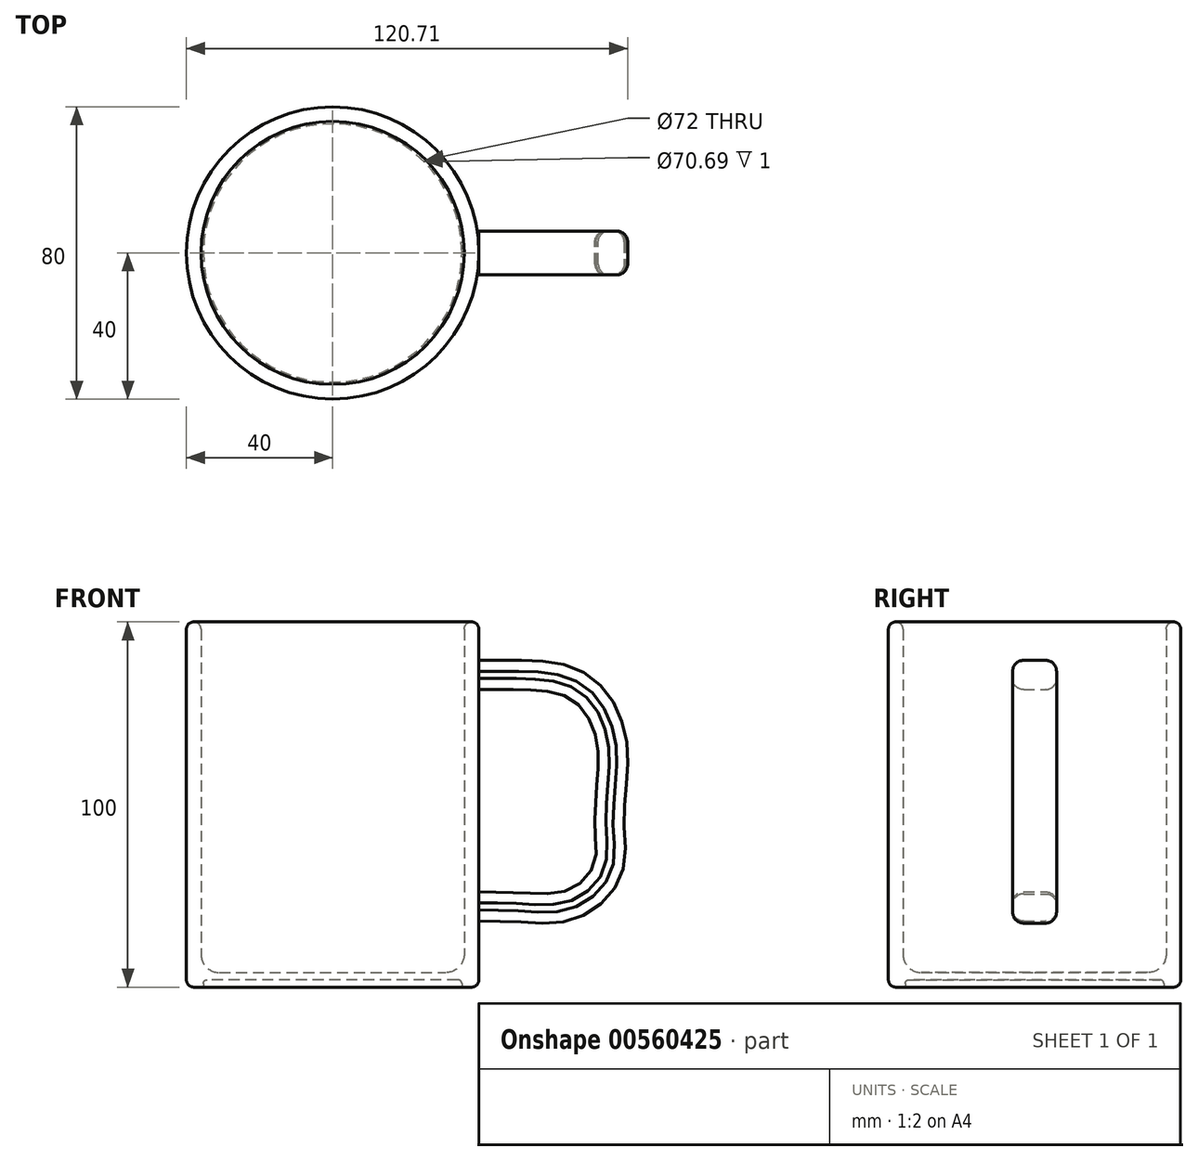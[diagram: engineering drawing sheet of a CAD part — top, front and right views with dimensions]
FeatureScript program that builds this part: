
annotation { "Feature Type Name" : "Feature", "Feature Type Description" : "" }
export const myFeature = defineFeature(function(context is Context, id is Id, definition is map)
    precondition{}
    {
        {
            var Q0;
            Q0=qCreatedBy(makeId("Front.planeOp"),FACE);
            var sketch = newSketch(context, id + "F0", { "sketchPlane" : qUnion([Q0])});
            skLineSegment(sketch, "E0.bottom", {"start": v(0, 0) * mm, "end": v(40, 0) * mm});
            skLineSegment(sketch, "E0.top", {"start": v(0, 100) * mm, "end": v(40, 100) * mm});
            skLineSegment(sketch, "E0.left", {"start": v(0, 0) * mm, "end": v(0, 100) * mm});
            skLineSegment(sketch, "E0.right", {"start": v(40, 0) * mm, "end": v(40, 100) * mm});
            skFitSpline(sketch, "E1", {"points": [v(31.21, 81.47) * mm, v(49.43, 81.47) * mm, v(64.9, 79.06) * mm, v(71.77, 69.44) * mm, v(72.45, 57.4) * mm, v(71.77, 43.32) * mm, v(71.42, 33.35) * mm, v(64.2, 26.48) * mm, v(52.18, 25.8) * mm, v(32.59, 26.13) * mm], "startDerivative": vector(140.72, 0.24) * mm, "endDerivative": vector(-154.35, 0.43) * mm});
            skFitSpline(sketch, "E2.0", {"points": [v(31.2, 89.47) * mm, v(32.66, 89.47) * mm, v(35.6, 89.47) * mm, v(39.27, 89.48) * mm, v(42.22, 89.48) * mm, v(44.44, 89.48) * mm, v(46.66, 89.47) * mm, v(48.52, 89.47) * mm, v(50, 89.46) * mm, v(51.15, 89.46) * mm, v(52.32, 89.45) * mm, v(53.91, 89.41) * mm, v(55.95, 89.33) * mm, v(58.48, 89.13) * mm, v(61.07, 88.77) * mm, v(63.29, 88.27) * mm, v(65.09, 87.71) * mm, v(66.45, 87.2) * mm, v(67.58, 86.7) * mm, v(68.48, 86.22) * mm, v(69.38, 85.7) * mm, v(70.45, 85.01) * mm, v(71.64, 84.1) * mm, v(72.74, 83.13) * mm, v(74.08, 81.76) * mm, v(75.55, 79.95) * mm, v(77, 77.66) * mm, v(78.17, 75.32) * mm, v(79.1, 72.93) * mm, v(79.78, 70.54) * mm, v(80.4, 67.39) * mm, v(80.7, 63.6) * mm, v(80.63, 60.08) * mm, v(80.5, 57.7) * mm, v(80.4, 56.38) * mm, v(80.25, 54.39) * mm, v(80.07, 52.1) * mm, v(79.9, 49.56) * mm, v(79.8, 47.74) * mm, v(79.74, 46.3) * mm, v(79.73, 45.2) * mm, v(79.74, 44.53) * mm, v(79.75, 44.02) * mm, v(79.76, 43.65) * mm, v(79.77, 43.29) * mm, v(79.8, 42.78) * mm, v(79.84, 42.11) * mm, v(79.92, 40.99) * mm, v(80.03, 39.45) * mm, v(80.1, 37.36) * mm, v(80.01, 35.37) * mm, v(79.77, 33.64) * mm, v(79.48, 32.28) * mm, v(79.13, 31.12) * mm, v(78.78, 30.18) * mm, v(78.39, 29.27) * mm, v(77.84, 28.19) * mm, v(76.85, 26.57) * mm, v(75.43, 24.73) * mm, v(73.48, 22.81) * mm, v(71.68, 21.43) * mm, v(70.13, 20.46) * mm, v(68.92, 19.8) * mm, v(67.66, 19.23) * mm, v(66.34, 18.73) * mm, v(65.03, 18.34) * mm, v(63.31, 17.94) * mm, v(61.23, 17.64) * mm, v(58.89, 17.52) * mm, v(56.69, 17.54) * mm, v(54.6, 17.64) * mm, v(53.1, 17.73) * mm, v(52.13, 17.78) * mm, v(51.48, 17.82) * mm, v(50.67, 17.86) * mm, v(49.66, 17.9) * mm, v(48.28, 17.95) * mm, v(45.8, 18.02) * mm, v(42.06, 18.09) * mm, v(37.38, 18.12) * mm, v(34.17, 18.13) * mm, v(32.56, 18.13) * mm]});
            skLineSegment(sketch, "E3", {"start": v(31.2, 89.47) * mm, "end": v(31.21, 81.47) * mm});
            skLineSegment(sketch, "E4", {"start": v(32.59, 26.13) * mm, "end": v(32.56, 18.13) * mm});
            skSolve(sketch);
        }
        {
            var Q0;
            {var subQ9=sQuery(id+"F0.wireOp",EDGE,"E0.bottom");Q0=makeQuery(id+"F0.imprint","IMPRINT",FACE,{"disambiguationData":[TD([[makeQuery(id+"F0.imprint","IMPRINT",EDGE,{"derivedFrom":subQ9}),1.0]])]});}
            var Q1;
            {var subQ5=sQuery(id+"F0.wireOp",EDGE,"E3");Q1=makeQuery(id+"F0.imprint","IMPRINT",FACE,{"disambiguationData":[TD([[makeQuery(id+"F0.imprint","IMPRINT",EDGE,{"derivedFrom":subQ5}),1.0]])]});}
            var Q2;
            {var subQ5=sQuery(id+"F0.wireOp",EDGE,"E4");Q2=makeQuery(id+"F0.imprint","IMPRINT",FACE,{"disambiguationData":[TD([[makeQuery(id+"F0.imprint","IMPRINT",EDGE,{"derivedFrom":subQ5}),1.0]])]});}
            var Q3;
            Q3=sQuery(id+"F0.wireOp",EDGE,"E0.left");
            revolve(context, id + "F1", {"entities" : qUnion([Q0, Q1, Q2]), "axis" : qUnion([Q3]), "revolveType" : RevolveType.FULL});
        }
        {
            var Q0;
            {var subQ0=sQuery(id+"F0.wireOp",EDGE,"E2.0");var subQ1=sQuery(id+"F0.wireOp",EDGE,"E0.right");var subQ2=makeQuery(id+"F0.imprint","INTERSECT",VERTEX,{"disambiguationData":[OD(0.0)],"derivedFrom":[subQ1,subQ0]});Q0=makeQuery(id+"F0.imprint","IMPRINT",FACE,{"disambiguationData":[TD([[makeQuery(id+"F0.imprint","IMPRINT",EDGE,{"disambiguationData":[TD([[subQ2,-1.0]])],"derivedFrom":subQ1}),-1.0]])]});}
            extrude(context, id + "F2", {"entities" : qUnion([Q0]), "operationType" : NewBodyOperationType.ADD, "endBound" : BoundingType.SYMMETRIC, "depth" : 12 * mm, "offsetDistance" : 25 * mm});
        }
        {
            var Q0;
            Q0=makeQuery(id+"F2.opExtrude","CAP_EDGE",EDGE,{"disambiguationData":[OSD([sQuery(id+"F0.wireOp",EDGE,"E2.0")])],"isStart":false});
            var Q1;
            Q1=makeQuery(id+"F2.opExtrude","CAP_EDGE",EDGE,{"disambiguationData":[OSD([sQuery(id+"F0.wireOp",EDGE,"E1")])],"isStart":false});
            var Q2;
            Q2=makeQuery(id+"F2.opExtrude","CAP_EDGE",EDGE,{"disambiguationData":[OSD([sQuery(id+"F0.wireOp",EDGE,"E2.0")])],"isStart":true});
            var Q3;
            Q3=makeQuery(id+"F2.opExtrude","CAP_EDGE",EDGE,{"disambiguationData":[OSD([sQuery(id+"F0.wireOp",EDGE,"E1")])],"isStart":true});
            fillet(context, id + "F3", {"entities" : qUnion([Q0, Q1, Q2, Q3]), "radius" : 3 * mm, "tangentPropagation" : true, "allowEdgeOverflow" : false});
        }
        {
            var Q0;
            Q0=makeQuery(id+"F1.opRevolve","SWEPT_FACE",FACE,{"disambiguationData":[OSD([sQuery(id+"F0.wireOp",EDGE,"E0.top")])]});
            shell(context, id + "F4", {"entities" : qUnion([Q0]), "thickness" : 4 * mm});
        }
        {
            var Q0;
            Q0=makeQuery(id+"F4.opShell","OFFSET_EDGE",EDGE,{"disambiguationData":[OSD([sQuery(id+"F0.wireOp",EDGE,"E0.top"),sQuery(id+"F0.wireOp",EDGE,"E0.right")])]});
            var Q1;
            Q1=makeQuery(id+"F1.opRevolve","SWEPT_EDGE",EDGE,{"disambiguationData":[OSD([sQuery(id+"F0.wireOp",EDGE,"E0.top"),sQuery(id+"F0.wireOp",EDGE,"E0.right")])]});
            fillet(context, id + "F5", {"entities" : qUnion([Q0, Q1]), "radius" : 2 * mm, "tangentPropagation" : true, "allowEdgeOverflow" : false});
        }
        {
            var Q0;
            Q0=makeQuery(id+"F4.opShell","OFFSET_EDGE",EDGE,{"disambiguationData":[OSD([sQuery(id+"F0.wireOp",EDGE,"E0.bottom"),sQuery(id+"F0.wireOp",EDGE,"E0.right")])]});
            fillet(context, id + "F6", {"entities" : qUnion([Q0]), "radius" : 5 * mm, "tangentPropagation" : true, "allowEdgeOverflow" : false});
        }
        {
            var Q0;
            Q0=qCreatedBy(makeId("Top.planeOp"),FACE);
            var sketch = newSketch(context, id + "F7", { "sketchPlane" : qUnion([Q0])});
            skCircle(sketch, "E5", {"center": v(0, 0) * mm, "radius": 35.35 * mm});
            skSolve(sketch);
        }
        {
            var Q0;
            Q0=makeQuery(id+"F7.imprint","IMPRINT",FACE,{"disambiguationData":[TD([[makeQuery(id+"F7.imprint","IMPRINT",EDGE,{"derivedFrom":sQuery(id+"F7.wireOp",EDGE,"E5")}),1.0]])]});
            var Q1;
            Q1=sQuery(id+"F7.wireOp",EDGE,"E5");
            extrude(context, id + "F8", {"entities" : qUnion([Q0]), "operationType" : NewBodyOperationType.REMOVE, "surfaceEntities" : qUnion([Q1]), "depth" : 2 * mm, "offsetDistance" : 25 * mm});
        }
        {
            var Q0;
            Q0=makeQuery(id+"F8.boolean.opBoolean","COPY",EDGE,{"derivedFrom":makeQuery(id+"F8.opExtrude","CAP_EDGE",EDGE,{"disambiguationData":[OSD([sQuery(id+"F7.wireOp",EDGE,"E5")])],"isStart":false})});
            var Q1;
            Q1=makeQuery(id+"F8.boolean.opBoolean","COPY",EDGE,{"derivedFrom":makeQuery(id+"F8.opExtrude","CAP_EDGE",EDGE,{"disambiguationData":[OSD([sQuery(id+"F7.wireOp",EDGE,"E5")])],"isStart":true})});
            fillet(context, id + "F9", {"entities" : qUnion([Q0, Q1]), "radius" : 1 * mm, "tangentPropagation" : true, "allowEdgeOverflow" : false});
        }
        {
            var Q0;
            Q0=makeQuery(id+"F9.opFillet","BLEND_EDGE",EDGE,{"blendedFrom":[makeQuery(id+"F8.boolean.opBoolean","COPY",EDGE,{"derivedFrom":makeQuery(id+"F8.opExtrude","CAP_EDGE",EDGE,{"disambiguationData":[OSD([sQuery(id+"F7.wireOp",EDGE,"E5")])],"isStart":true})}),makeQuery(id+"F1.opRevolve","SWEPT_FACE",FACE,{"disambiguationData":[OSD([sQuery(id+"F0.wireOp",EDGE,"E0.bottom")])]})],"blendedInto":[makeQuery(id+"F1.opRevolve","SWEPT_FACE",FACE,{"disambiguationData":[OSD([sQuery(id+"F0.wireOp",EDGE,"E0.bottom")])]})]});
            var Q1;
            Q1=makeQuery(id+"F1.opRevolve","SWEPT_EDGE",EDGE,{"disambiguationData":[OSD([sQuery(id+"F0.wireOp",EDGE,"E0.bottom"),sQuery(id+"F0.wireOp",EDGE,"E0.right")])]});
            fillet(context, id + "F10", {"entities" : qUnion([Q0, Q1]), "radius" : 2 * mm, "tangentPropagation" : true, "allowEdgeOverflow" : false});
        }
    });
